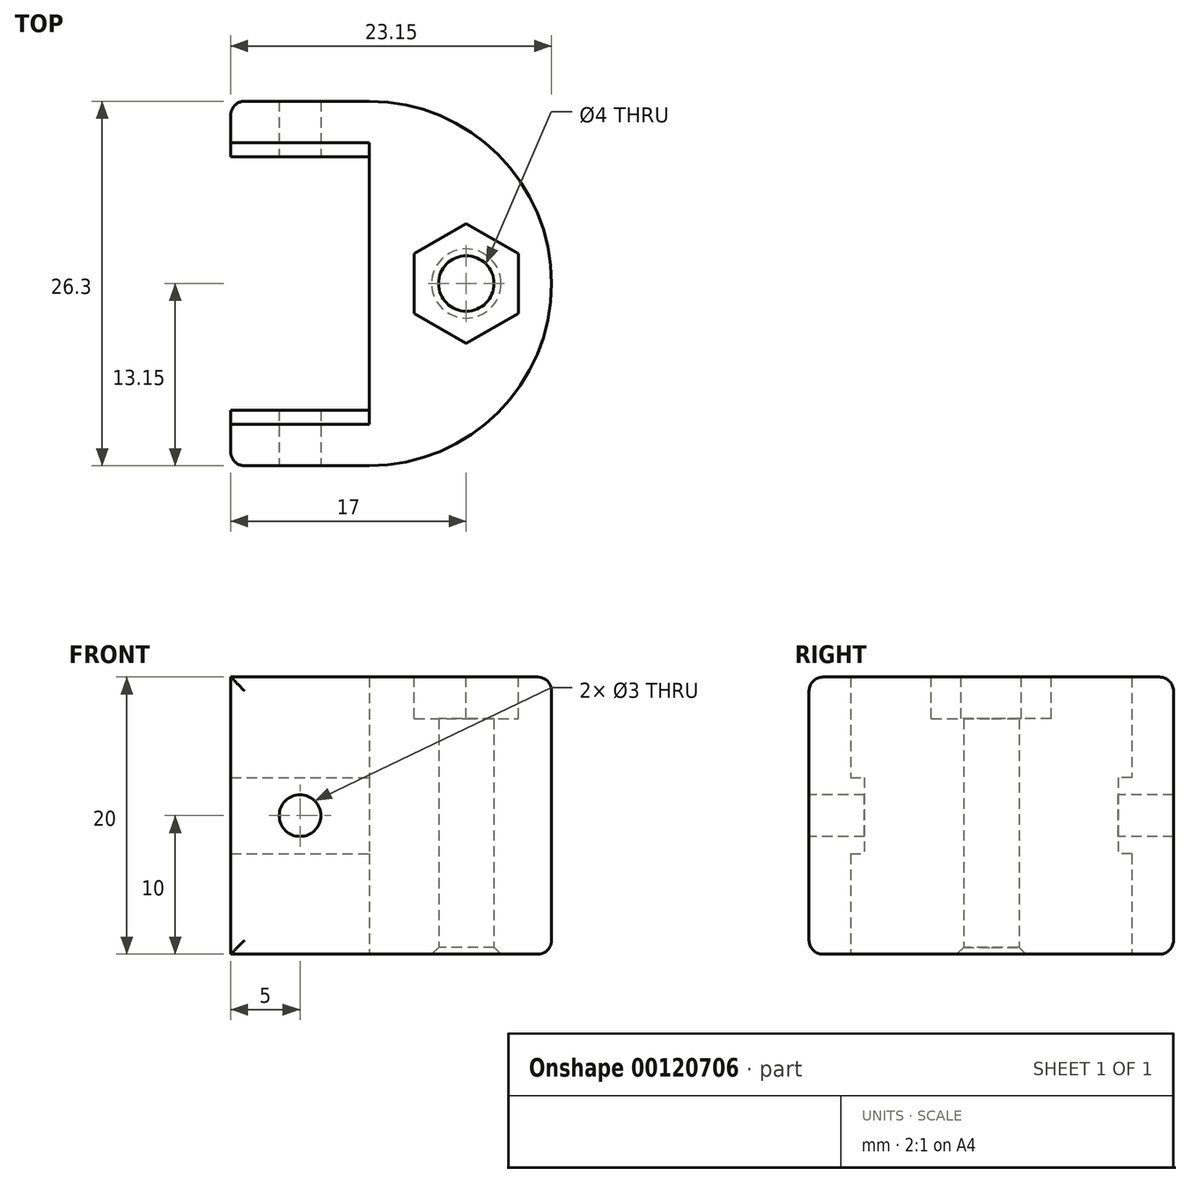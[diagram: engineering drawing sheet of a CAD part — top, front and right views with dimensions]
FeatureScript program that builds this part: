
annotation { "Feature Type Name" : "Feature", "Feature Type Description" : "" }
export const myFeature = defineFeature(function(context is Context, id is Id, definition is map)
    precondition{}
    {
        {
            var Q0;
            Q0=qCreatedBy(makeId("Top.planeOp"),FACE);
            var sketch = newSketch(context, id + "F0", { "sketchPlane" : qUnion([Q0])});
            skLineSegment(sketch, "E0", {"start": v(0, 0) * mm, "end": v(0, 3) * mm});
            skLineSegment(sketch, "E1", {"start": v(0, 3) * mm, "end": v(10, 3) * mm});
            skLineSegment(sketch, "E2", {"start": v(10, 3) * mm, "end": v(10, 23.3) * mm});
            skLineSegment(sketch, "E3", {"start": v(10, 23.3) * mm, "end": v(0, 23.3) * mm});
            skLineSegment(sketch, "E4", {"start": v(0, 23.3) * mm, "end": v(0, 26.3) * mm});
            skLineSegment(sketch, "E5", {"start": v(0, 26.3) * mm, "end": v(10, 26.3) * mm});
            skLineSegment(sketch, "E6", {"start": v(0, 0) * mm, "end": v(10, 0) * mm});
            skArc(sketch, "E7", {"start": v(10, 26.3) * mm, "mid": v(23.15, 13.15) * mm, "end": v(10, 0) * mm});
            skCircle(sketch, "E8", {"center": v(17, 13.15) * mm, "radius": 2 * mm});
            skSolve(sketch);
        }
        {
            var Q0;
            Q0=makeQuery(id+"F0.imprint","IMPRINT",FACE,{"disambiguationData":[TD([[makeQuery(id+"F0.imprint","IMPRINT",EDGE,{"derivedFrom":sQuery(id+"F0.wireOp",EDGE,"E0")}),-1.0]])]});
            extrude(context, id + "F1", {"entities" : qUnion([Q0]), "depth" : 20 * mm});
        }
        {
            var Q0;
            Q0=makeQuery(id+"F1.opExtrude","SWEPT_FACE",FACE,{"disambiguationData":[OSD([sQuery(id+"F0.wireOp",EDGE,"E2")])]});
            var sketch = newSketch(context, id + "F2", { "sketchPlane" : qUnion([Q0])});
            skLineSegment(sketch, "E9.bottom", {"start": v(-23.3, 12.75) * mm, "end": v(-22.3, 12.75) * mm});
            skLineSegment(sketch, "E9.top", {"start": v(-23.3, 7.25) * mm, "end": v(-22.3, 7.25) * mm});
            skLineSegment(sketch, "E9.left", {"start": v(-23.3, 12.75) * mm, "end": v(-23.3, 7.25) * mm});
            skLineSegment(sketch, "E9.right", {"start": v(-22.3, 12.75) * mm, "end": v(-22.3, 7.25) * mm});
            skLineSegment(sketch, "E10.bottom", {"start": v(-3, 12.75) * mm, "end": v(-4, 12.75) * mm});
            skLineSegment(sketch, "E10.top", {"start": v(-3, 7.25) * mm, "end": v(-4, 7.25) * mm});
            skLineSegment(sketch, "E10.left", {"start": v(-3, 12.75) * mm, "end": v(-3, 7.25) * mm});
            skLineSegment(sketch, "E10.right", {"start": v(-4, 12.75) * mm, "end": v(-4, 7.25) * mm});
            skSolve(sketch);
        }
        {
            var Q0;
            Q0 = qSketchRegion(id + "F2", true);
            var Q1;
            Q1=makeQuery(id+"F1.opExtrude","SWEPT_FACE",FACE,{"disambiguationData":[OSD([sQuery(id+"F0.wireOp",EDGE,"E4")])]});
            extrude(context, id + "F3", {"entities" : qUnion([Q0]), "operationType" : NewBodyOperationType.ADD, "endBound" : BoundingType.UP_TO_SURFACE, "endBoundEntityFace" : qUnion([Q1]), "depth" : 25 * mm});
        }
        {
            var Q0;
            Q0=makeQuery(id+"F1.opExtrude","SWEPT_FACE",FACE,{"disambiguationData":[OSD([sQuery(id+"F0.wireOp",EDGE,"E6")])]});
            var sketch = newSketch(context, id + "F4", { "sketchPlane" : qUnion([Q0])});
            skCircle(sketch, "E11", {"center": v(5, 10) * mm, "radius": 1.5 * mm});
            skPoint(sketch, "E11.centerSnap0", {"position": v(5, 0) * mm});
            skPoint(sketch, "E11.centerSnap1", {"position": v(0, 10) * mm});
            skSolve(sketch);
        }
        {
            var Q0;
            Q0=qSketchRegion(id+"F4",true);
            extrude(context, id + "F5", {"entities" : qUnion([Q0]), "operationType" : NewBodyOperationType.REMOVE, "endBound" : BoundingType.THROUGH_ALL, "oppositeDirection" : true, "depth" : 25 * mm});
        }
        {
            var Q0;
            Q0=makeQuery(id+"F1.opExtrude","CAP_EDGE",EDGE,{"disambiguationData":[OSD([sQuery(id+"F0.wireOp",EDGE,"E8")])],"isStart":true});
            chamfer(context, id + "F6", {"entities" : qUnion([Q0]), "width" : 0.5 * mm, "tangentPropagation" : true});
        }
        {
            var Q0;
            Q0=makeQuery(id+"F1.opExtrude","CAP_EDGE",EDGE,{"disambiguationData":[OSD([sQuery(id+"F0.wireOp",EDGE,"E7")])],"isStart":false});
            var Q1;
            Q1=makeQuery(id+"F1.opExtrude","CAP_EDGE",EDGE,{"disambiguationData":[OSD([sQuery(id+"F0.wireOp",EDGE,"E7")])],"isStart":true});
            var Q2;
            Q2=makeQuery(id+"F1.opExtrude","SWEPT_EDGE",EDGE,{"disambiguationData":[OSD([sQuery(id+"F0.wireOp",EDGE,"E0"),sQuery(id+"F0.wireOp",EDGE,"E6")])]});
            var Q3;
            Q3=makeQuery(id+"F1.opExtrude","SWEPT_EDGE",EDGE,{"disambiguationData":[OSD([sQuery(id+"F0.wireOp",EDGE,"E4"),sQuery(id+"F0.wireOp",EDGE,"E5")])]});
            fillet(context, id + "F7", {"entities" : qUnion([Q0, Q1, Q2, Q3]), "radius" : 1 * mm, "tangentPropagation" : true, "allowEdgeOverflow" : false});
        }
        {
            var Q0;
            Q0=makeQuery(id+"F1.opExtrude","CAP_FACE",FACE,{"disambiguationData":[OSD([sQuery(id+"F0.wireOp",EDGE,"E0"),sQuery(id+"F0.wireOp",EDGE,"E1"),sQuery(id+"F0.wireOp",EDGE,"E2"),sQuery(id+"F0.wireOp",EDGE,"E3"),sQuery(id+"F0.wireOp",EDGE,"E4"),sQuery(id+"F0.wireOp",EDGE,"E5"),sQuery(id+"F0.wireOp",EDGE,"E6"),sQuery(id+"F0.wireOp",EDGE,"E7"),sQuery(id+"F0.wireOp",EDGE,"E8")])],"isStart":false});
            var sketch = newSketch(context, id + "F8", { "sketchPlane" : qUnion([Q0])});
            skCircle(sketch, "E12.cCircle", {"center": v(17, 13.15) * mm, "radius": 3.75 * mm, "construction": true});
            skLineSegment(sketch, "E12.0", {"start": v(20.75, 15.32) * mm, "end": v(20.75, 10.98) * mm});
            skLineSegment(sketch, "E12.1", {"start": v(20.75, 10.98) * mm, "end": v(17, 8.82) * mm});
            skLineSegment(sketch, "E12.2", {"start": v(17, 8.82) * mm, "end": v(13.25, 10.98) * mm});
            skLineSegment(sketch, "E12.3", {"start": v(13.25, 10.98) * mm, "end": v(13.25, 15.32) * mm});
            skLineSegment(sketch, "E12.4", {"start": v(13.25, 15.32) * mm, "end": v(17, 17.48) * mm});
            skLineSegment(sketch, "E12.5", {"start": v(17, 17.48) * mm, "end": v(20.75, 15.32) * mm});
            skPoint(sketch, "E12.0.midPoint", {"position": v(20.75, 13.15) * mm});
            skSolve(sketch);
        }
        {
            var Q0;
            Q0 = qSketchRegion(id + "F8", true);
            extrude(context, id + "F9", {"entities" : qUnion([Q0]), "operationType" : NewBodyOperationType.REMOVE, "oppositeDirection" : true, "depth" : 3 * mm});
        }
    });
